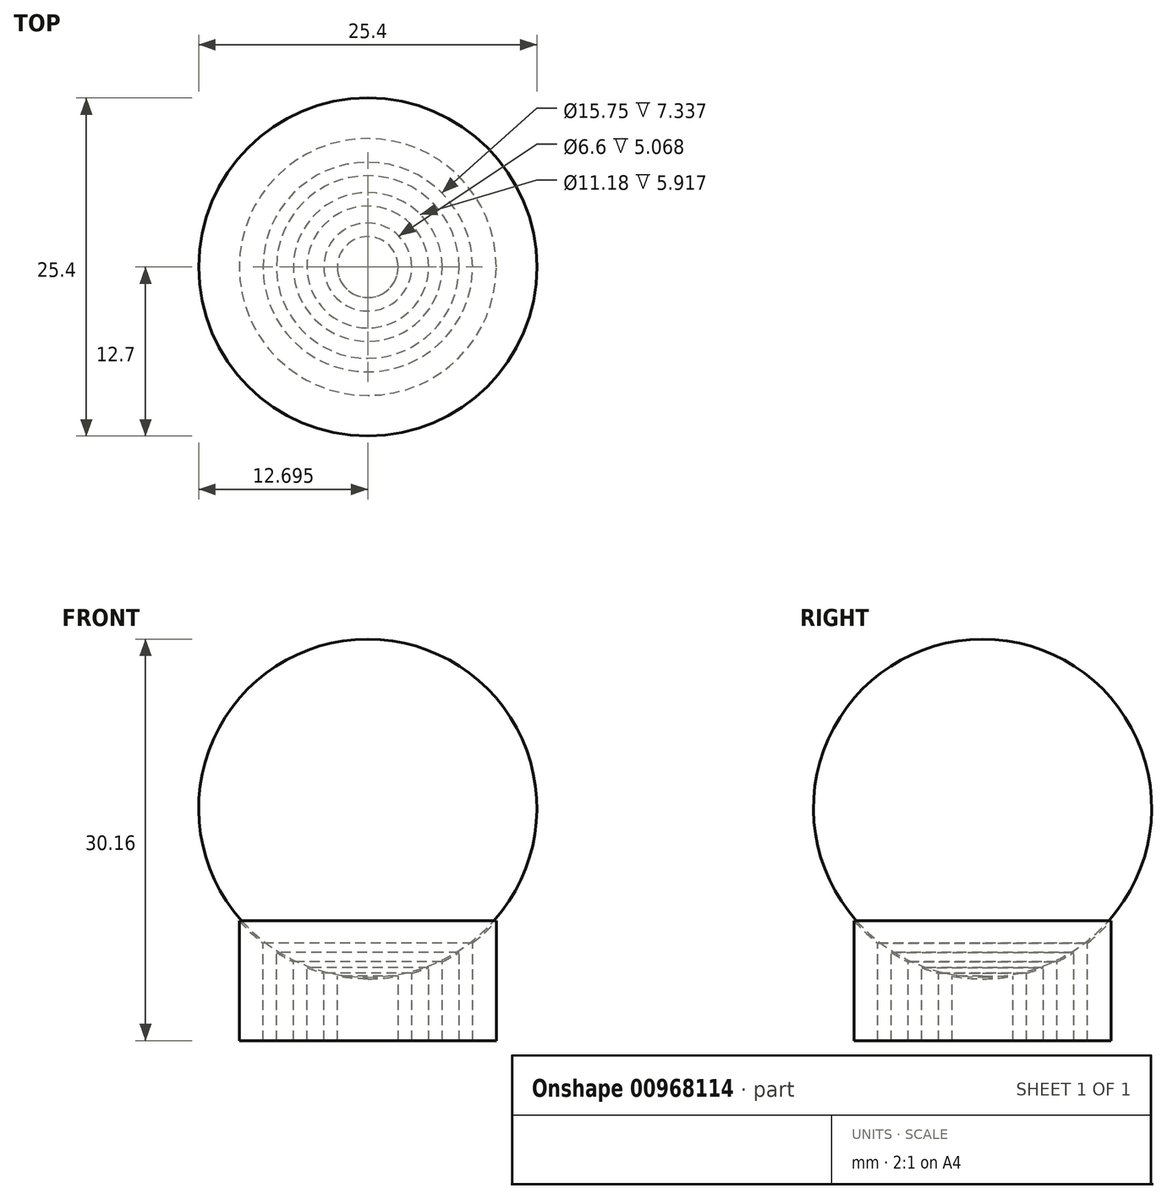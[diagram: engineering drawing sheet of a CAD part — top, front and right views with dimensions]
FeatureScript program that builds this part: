
annotation { "Feature Type Name" : "Feature", "Feature Type Description" : "" }
export const myFeature = defineFeature(function(context is Context, id is Id, definition is map)
    precondition{}
    {
        {
            var Q0;
            Q0=qCreatedBy(makeId("Front.planeOp"),FACE);
            var sketch = newSketch(context, id + "F0", { "sketchPlane" : qUnion([Q0])});
            skLineSegment(sketch, "E0", {"start": v(38.1, 17.46) * mm, "end": v(38.1, -17.46) * mm});
            skCircle(sketch, "E1", {"center": v(55.25, 0) * mm, "radius": 12.7 * mm, "construction": true});
            skArc(sketch, "E2", {"start": v(44.45, 8.87) * mm, "mid": v(41.27, 0) * mm, "end": v(44.45, -8.87) * mm});
            skLineSegment(sketch, "E3", {"start": v(72.4, 17.46) * mm, "end": v(72.4, -17.46) * mm});
            skLineSegment(sketch, "E4", {"start": v(38.1, 17.46) * mm, "end": v(44.45, 17.46) * mm});
            skLineSegment(sketch, "E5", {"start": v(44.45, 17.46) * mm, "end": v(44.45, 8.87) * mm});
            skLineSegment(sketch, "E6", {"start": v(38.1, -17.46) * mm, "end": v(44.45, -17.46) * mm});
            skLineSegment(sketch, "E7", {"start": v(44.45, -17.46) * mm, "end": v(44.45, -8.87) * mm});
            skLineSegment(sketch, "E8", {"start": v(72.4, 17.46) * mm, "end": v(66.04, 17.46) * mm});
            skLineSegment(sketch, "E9", {"start": v(66.04, 17.46) * mm, "end": v(66.04, 8.87) * mm});
            skLineSegment(sketch, "E10", {"start": v(72.4, -17.46) * mm, "end": v(66.04, -17.46) * mm});
            skLineSegment(sketch, "E11", {"start": v(66.04, -17.46) * mm, "end": v(66.04, -8.87) * mm});
            skArc(sketch, "E12.trimOffspring", {"start": v(66.04, -8.87) * mm, "mid": v(69.22, 0) * mm, "end": v(66.04, 8.87) * mm});
            skLineSegment(sketch, "E13", {"start": v(55.31, -12.7) * mm, "end": v(47.08, -12.7) * mm, "construction": true});
            skSolve(sketch);
        }
        {
            var Q0;
            Q0=qCreatedBy(makeId("Front.planeOp"),FACE);
            var sketch = newSketch(context, id + "F1", { "sketchPlane" : qUnion([Q0])});
            skLineSegment(sketch, "E14", {"start": v(55.25, 12.7) * mm, "end": v(55.25, -12.45) * mm});
            skArc(sketch, "E15", {"start": v(55.25, 12.7) * mm, "mid": v(67.9, 1.15) * mm, "end": v(57.53, -12.5) * mm});
            skPoint(sketch, "E16.orphan", {"position": v(55.25, -12.7) * mm});
            skLineSegment(sketch, "E17", {"start": v(57.53, -12.62) * mm, "end": v(57.53, -17.46) * mm});
            skLineSegment(sketch, "E18", {"start": v(55.25, -12.45) * mm, "end": v(55.25, -12.7) * mm});
            skLineSegment(sketch, "E19", {"start": v(55.25, -17.46) * mm, "end": v(57.53, -17.46) * mm});
            skArc(sketch, "E20", {"start": v(57.53, -12.5) * mm, "mid": v(56.4, -12.65) * mm, "end": v(55.25, -12.7) * mm});
            skArc(sketch, "E21", {"start": v(55.25, -12.83) * mm, "mid": v(56.4, -12.78) * mm, "end": v(57.53, -12.62) * mm});
            skLineSegment(sketch, "E22.trimOffspring", {"start": v(55.25, -12.83) * mm, "end": v(55.25, -17.46) * mm});
            skArc(sketch, "E23", {"start": v(58.55, -12.4) * mm, "mid": v(59.19, -12.2) * mm, "end": v(59.82, -11.98) * mm});
            skLineSegment(sketch, "E24", {"start": v(58.55, -12.4) * mm, "end": v(58.55, -17.46) * mm});
            skLineSegment(sketch, "E25", {"start": v(58.55, -17.46) * mm, "end": v(59.82, -17.46) * mm});
            skLineSegment(sketch, "E26", {"start": v(59.82, -17.46) * mm, "end": v(59.82, -11.98) * mm});
            skArc(sketch, "E27", {"start": v(60.83, -11.55) * mm, "mid": v(61.48, -11.21) * mm, "end": v(62.1, -10.84) * mm});
            skLineSegment(sketch, "E28", {"start": v(60.83, -11.55) * mm, "end": v(60.83, -17.46) * mm});
            skLineSegment(sketch, "E29", {"start": v(60.83, -17.46) * mm, "end": v(62.1, -17.46) * mm});
            skLineSegment(sketch, "E30", {"start": v(62.1, -17.46) * mm, "end": v(62.1, -10.84) * mm});
            skArc(sketch, "E31", {"start": v(63.12, -10.13) * mm, "mid": v(64.05, -9.33) * mm, "end": v(64.9, -8.45) * mm});
            skLineSegment(sketch, "E32", {"start": v(63.12, -10.13) * mm, "end": v(63.12, -17.46) * mm});
            skLineSegment(sketch, "E33", {"start": v(63.12, -17.46) * mm, "end": v(64.9, -17.46) * mm});
            skLineSegment(sketch, "E34", {"start": v(64.9, -17.46) * mm, "end": v(64.9, -8.45) * mm});
            skSolve(sketch);
        }
        {
            var Q0;
            Q0=qCreatedBy(makeId("Front.planeOp"),FACE);
            var sketch = newSketch(context, id + "F2", { "sketchPlane" : qUnion([Q0])});
            skLineSegment(sketch, "E35", {"start": v(55.25, 25) * mm, "end": v(55.25, -25.66) * mm});
            skSolve(sketch);
        }
        {
            var Q0;
            Q0=qSketchRegion(id+"F1",true);
            var Q1;
            Q1=sQuery(id+"F2.wireOp",EDGE,"E35");
            revolve(context, id + "F3", {"surfaceOperationType" : NewSurfaceOperationType.NEW, "entities" : qUnion([Q0]), "axis" : qUnion([Q1]), "revolveType" : RevolveType.FULL});
        }
    });
